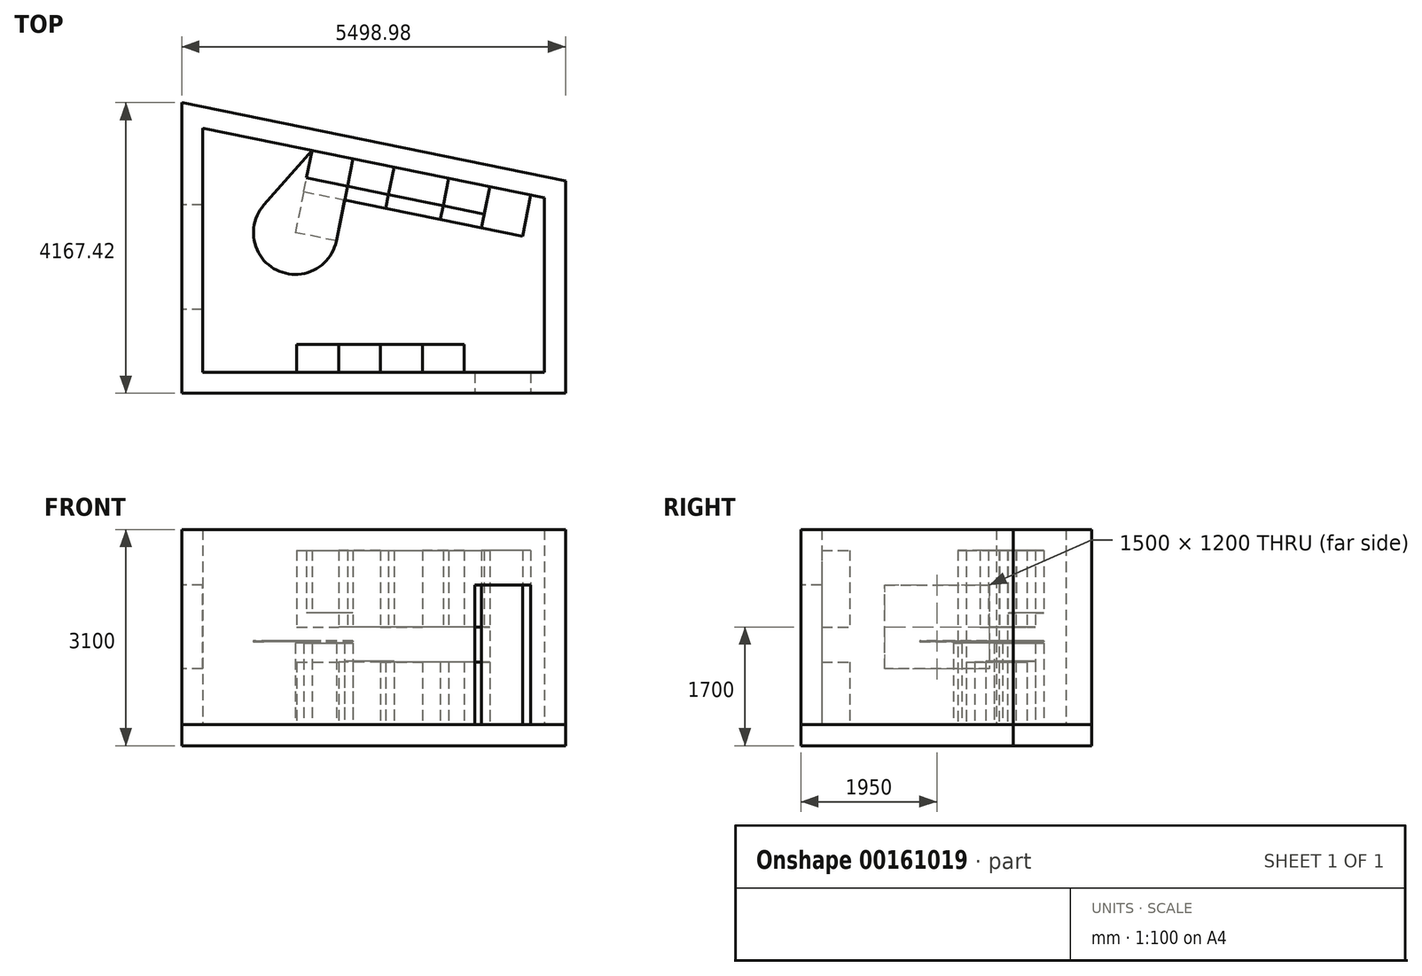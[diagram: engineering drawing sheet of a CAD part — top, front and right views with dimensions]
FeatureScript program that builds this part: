
annotation { "Feature Type Name" : "Feature", "Feature Type Description" : "" }
export const myFeature = defineFeature(function(context is Context, id is Id, definition is map)
    precondition{}
    {
        {
            var Q0;
            Q0=qCreatedBy(makeId("Top.planeOp"),FACE);
            var sketch = newSketch(context, id + "F0", { "sketchPlane" : qUnion([Q0])});
            skLineSegment(sketch, "E0", {"start": v(-2449.49, -1250) * mm, "end": v(2449.49, -1250) * mm});
            skLineSegment(sketch, "E1", {"start": v(2449.49, -1250) * mm, "end": v(2449.49, 1250) * mm});
            skLineSegment(sketch, "E2", {"start": v(2449.49, 1250) * mm, "end": v(-2449.49, 2250) * mm});
            skLineSegment(sketch, "E3", {"start": v(-2449.49, 2250) * mm, "end": v(-2449.49, -1250) * mm});
            skPoint(sketch, "E4", {"position": v(2449.49, 0) * mm});
            skLineSegment(sketch, "E5", {"start": v(2449.49, 0) * mm, "end": v(-2449.49, 0) * mm, "construction": true});
            skPoint(sketch, "E6", {"position": v(0, 0) * mm});
            skLineSegment(sketch, "E7.0", {"start": v(2749.49, 1494.95) * mm, "end": v(-2749.49, 2617.42) * mm});
            skLineSegment(sketch, "E7.1", {"start": v(2749.49, -1550) * mm, "end": v(2749.49, 1494.95) * mm});
            skLineSegment(sketch, "E7.2", {"start": v(-2749.49, -1550) * mm, "end": v(2749.49, -1550) * mm});
            skLineSegment(sketch, "E7.3", {"start": v(-2749.49, 2617.42) * mm, "end": v(-2749.49, -1550) * mm});
            skLineSegment(sketch, "E8", {"start": v(-2449.49, -250) * mm, "end": v(-2749.49, -250) * mm});
            skLineSegment(sketch, "E9", {"start": v(-2449.49, 1250) * mm, "end": v(-2749.49, 1250) * mm});
            skLineSegment(sketch, "E10", {"start": v(2249.49, -1250) * mm, "end": v(2249.49, -1550) * mm});
            skLineSegment(sketch, "E11", {"start": v(1449.49, -1250) * mm, "end": v(1449.49, -1550) * mm});
            skSolve(sketch);
        }
        {
            var Q0;
            {var subQ0=sQuery(id+"F0.wireOp",EDGE,"E8");Q0=makeQuery(id+"F0.imprint","IMPRINT",FACE,{"disambiguationData":[TD([[makeQuery(id+"F0.imprint","IMPRINT",EDGE,{"derivedFrom":subQ0}),-1.0]])]});}
            var Q1;
            {var subQ0=sQuery(id+"F0.wireOp",EDGE,"E1");Q1=makeQuery(id+"F0.imprint","IMPRINT",FACE,{"disambiguationData":[TD([[makeQuery(id+"F0.imprint","IMPRINT",EDGE,{"derivedFrom":subQ0}),1.0]])]});}
            var Q2;
            {var subQ6=sQuery(id+"F0.wireOp",EDGE,"E1");Q2=makeQuery(id+"F0.imprint","IMPRINT",FACE,{"disambiguationData":[TD([[makeQuery(id+"F0.imprint","IMPRINT",EDGE,{"derivedFrom":subQ6}),-1.0]])]});}
            var Q3;
            {var subQ0=sQuery(id+"F0.wireOp",EDGE,"E10");Q3=makeQuery(id+"F0.imprint","IMPRINT",FACE,{"disambiguationData":[TD([[makeQuery(id+"F0.imprint","IMPRINT",EDGE,{"derivedFrom":subQ0}),-1.0]])]});}
            var Q4;
            {var subQ3=sQuery(id+"F0.wireOp",EDGE,"E8");Q4=makeQuery(id+"F0.imprint","IMPRINT",FACE,{"disambiguationData":[TD([[makeQuery(id+"F0.imprint","IMPRINT",EDGE,{"derivedFrom":subQ3}),1.0]])]});}
            extrude(context, id + "F1", {"entities" : qUnion([Q0, Q1, Q2, Q3, Q4]), "oppositeDirection" : true, "depth" : 300 * mm});
        }
        {
            var Q0;
            {var subQ3=sQuery(id+"F0.wireOp",EDGE,"E8");Q0=makeQuery(id+"F0.imprint","IMPRINT",FACE,{"disambiguationData":[TD([[makeQuery(id+"F0.imprint","IMPRINT",EDGE,{"derivedFrom":subQ3}),1.0]])]});}
            var Q1;
            {var subQ0=sQuery(id+"F0.wireOp",EDGE,"E8");Q1=makeQuery(id+"F0.imprint","IMPRINT",FACE,{"disambiguationData":[TD([[makeQuery(id+"F0.imprint","IMPRINT",EDGE,{"derivedFrom":subQ0}),-1.0]])]});}
            var Q2;
            {var subQ6=sQuery(id+"F0.wireOp",EDGE,"E1");Q2=makeQuery(id+"F0.imprint","IMPRINT",FACE,{"disambiguationData":[TD([[makeQuery(id+"F0.imprint","IMPRINT",EDGE,{"derivedFrom":subQ6}),-1.0]])]});}
            var Q3;
            {var subQ0=sQuery(id+"F0.wireOp",EDGE,"E10");Q3=makeQuery(id+"F0.imprint","IMPRINT",FACE,{"disambiguationData":[TD([[makeQuery(id+"F0.imprint","IMPRINT",EDGE,{"derivedFrom":subQ0}),-1.0]])]});}
            extrude(context, id + "F2", {"entities" : qUnion([Q0, Q1, Q2, Q3]), "depth" : 2800 * mm});
        }
        {
            var Q0;
            {var subQ0=sQuery(id+"F0.wireOp",EDGE,"E10");Q0=makeQuery(id+"F0.imprint","IMPRINT",FACE,{"disambiguationData":[TD([[makeQuery(id+"F0.imprint","IMPRINT",EDGE,{"derivedFrom":subQ0}),-1.0]])]});}
            extrude(context, id + "F3", {"entities" : qUnion([Q0]), "operationType" : NewBodyOperationType.REMOVE, "depth" : 2000 * mm});
        }
        {
            var Q0;
            Q0=makeQuery(id+"F2.opExtrude","SWEPT_FACE",FACE,{"disambiguationData":[OSD([sQuery(id+"F0.wireOp",EDGE,"E7.3")])]});
            var sketch = newSketch(context, id + "F4", { "sketchPlane" : qUnion([Q0])});
            skLineSegment(sketch, "E12.0", {"start": v(1250, 2000) * mm, "end": v(1550, 2000) * mm});
            skLineSegment(sketch, "E13", {"start": v(350, 800) * mm, "end": v(350, 2000) * mm});
            skLineSegment(sketch, "E14", {"start": v(350, 2000) * mm, "end": v(-1150, 2000) * mm});
            skLineSegment(sketch, "E15", {"start": v(-1150, 2000) * mm, "end": v(-1150, 800) * mm});
            skLineSegment(sketch, "E16", {"start": v(-1150, 800) * mm, "end": v(350, 800) * mm});
            skSolve(sketch);
        }
        {
            var Q0;
            Q0=makeQuery(id+"F4.imprint","IMPRINT",FACE,{"disambiguationData":[TD([[makeQuery(id+"F4.imprint","IMPRINT",EDGE,{"derivedFrom":sQuery(id+"F4.wireOp",EDGE,"E13")}),1.0]])]});
            var Q1;
            Q1=makeQuery(id+"F2.opExtrude","SWEPT_FACE",FACE,{"disambiguationData":[OSD([sQuery(id+"F0.wireOp",EDGE,"E3")])]});
            extrude(context, id + "F5", {"entities" : qUnion([Q0]), "operationType" : NewBodyOperationType.REMOVE, "endBound" : BoundingType.UP_TO_SURFACE, "oppositeDirection" : true, "endBoundEntityFace" : qUnion([Q1]), "depth" : 25 * mm});
        }
        {
            var Q0;
            Q0=makeQuery(id+"F2.opExtrude","CAP_FACE",FACE,{"disambiguationData":[OSD([sQuery(id+"F0.wireOp",EDGE,"E0"),sQuery(id+"F0.wireOp",EDGE,"E1"),sQuery(id+"F0.wireOp",EDGE,"E2"),sQuery(id+"F0.wireOp",EDGE,"E3"),sQuery(id+"F0.wireOp",EDGE,"E7.0"),sQuery(id+"F0.wireOp",EDGE,"E7.1"),sQuery(id+"F0.wireOp",EDGE,"E7.2"),sQuery(id+"F0.wireOp",EDGE,"E7.3")])],"isStart":true});
            var sketch = newSketch(context, id + "F6", { "sketchPlane" : qUnion([Q0])});
            skLineSegment(sketch, "E17.0", {"start": v(2449.49, -1250) * mm, "end": v(-2449.49, -2250) * mm});
            skLineSegment(sketch, "E18.0", {"start": v(2449.49, 1250) * mm, "end": v(2449.49, -1250) * mm});
            skLineSegment(sketch, "E19.0", {"start": v(-2449.49, 1250) * mm, "end": v(1449.49, 1250) * mm});
            skLineSegment(sketch, "E20.0", {"start": v(1449.49, 1250) * mm, "end": v(1449.49, 1550) * mm});
            skLineSegment(sketch, "E21.0", {"start": v(-2449.49, -2250) * mm, "end": v(-2449.49, 1250) * mm});
            skLineSegment(sketch, "E22", {"start": v(2253.53, -1290) * mm, "end": v(2133.53, -702.12) * mm});
            skLineSegment(sketch, "E23", {"start": v(2133.53, -702.12) * mm, "end": v(-1001.82, -1342.12) * mm});
            skLineSegment(sketch, "E24", {"start": v(1545.65, -822.12) * mm, "end": v(1665.65, -1410) * mm});
            skLineSegment(sketch, "E25", {"start": v(1077.78, -1530) * mm, "end": v(957.78, -942.12) * mm});
            skLineSegment(sketch, "E26", {"start": v(293.94, -1690) * mm, "end": v(173.94, -1102.12) * mm});
            skLineSegment(sketch, "E27", {"start": v(-293.94, -1810) * mm, "end": v(-533.94, -634.24) * mm});
            skLineSegment(sketch, "E28", {"start": v(-881.82, -1930) * mm, "end": v(-1121.82, -754.24) * mm});
            skLineSegment(sketch, "E29", {"start": v(1299.49, 850) * mm, "end": v(-1100.51, 850) * mm});
            skLineSegment(sketch, "E30", {"start": v(1299.49, 1250) * mm, "end": v(1299.49, 850) * mm});
            skLineSegment(sketch, "E31", {"start": v(699.49, 1250) * mm, "end": v(699.49, 850) * mm});
            skLineSegment(sketch, "E32", {"start": v(99.49, 1250) * mm, "end": v(99.49, 850) * mm});
            skLineSegment(sketch, "E33", {"start": v(-500.51, 1250) * mm, "end": v(-500.51, 850) * mm});
            skPoint(sketch, "E34.orphan", {"position": v(1449.49, 850) * mm});
            skLineSegment(sketch, "E35", {"start": v(-1100.51, 850) * mm, "end": v(-1100.51, 1250) * mm});
            skCircle(sketch, "E36", {"center": v(-1121.82, -754.24) * mm, "radius": 600 * mm});
            skLineSegment(sketch, "E37", {"start": v(-881.82, -1930) * mm, "end": v(-1570.93, -1152.1) * mm});
            skLineSegment(sketch, "E38", {"start": v(-533.94, -634.24) * mm, "end": v(-1121.82, -754.24) * mm});
            skLineSegment(sketch, "E39", {"start": v(2173.53, -898.08) * mm, "end": v(-2449.49, -1841.75) * mm});
            skSolve(sketch);
        }
        {
            var Q0;
            {var subQ0=sQuery(id+"F6.wireOp",EDGE,"E22");Q0=makeQuery(id+"F6.imprint","IMPRINT",FACE,{"disambiguationData":[TD([[makeQuery(id+"F6.imprint","IMPRINT",EDGE,{"derivedFrom":subQ0}),1.0]])]});}
            extrude(context, id + "F7", {"entities" : qUnion([Q0]), "oppositeDirection" : true, "depth" : 2500 * mm});
        }
        {
            var Q0;
            {var subQ3=sQuery(id+"F6.wireOp",EDGE,"E38");Q0=makeQuery(id+"F6.imprint","IMPRINT",FACE,{"disambiguationData":[TD([[makeQuery(id+"F6.imprint","IMPRINT",EDGE,{"derivedFrom":subQ3}),1.0]])]});}
            var Q1;
            {var subQ1=sQuery(id+"F6.wireOp",EDGE,"E23");var subQ3=sQuery(id+"F6.wireOp",EDGE,"E27");var subQ4=makeQuery(id+"F6.imprint","INTERSECT",VERTEX,{"derivedFrom":[subQ1,subQ3]});Q1=makeQuery(id+"F6.imprint","IMPRINT",FACE,{"disambiguationData":[TD([[makeQuery(id+"F6.imprint","IMPRINT",EDGE,{"disambiguationData":[TD([[subQ4,-1.0]])],"derivedFrom":subQ1}),-1.0]])]});}
            extrude(context, id + "F8", {"entities" : qUnion([Q0, Q1]), "oppositeDirection" : true, "depth" : 1170 * mm});
        }
        {
            var Q0;
            {var subQ0=sQuery(id+"F6.wireOp",EDGE,"E30");Q0=makeQuery(id+"F6.imprint","IMPRINT",FACE,{"disambiguationData":[TD([[makeQuery(id+"F6.imprint","IMPRINT",EDGE,{"derivedFrom":subQ0}),-1.0]])]});}
            extrude(context, id + "F9", {"entities" : qUnion([Q0]), "oppositeDirection" : true, "depth" : 900 * mm});
        }
        {
            var Q0;
            {var subQ0=sQuery(id+"F6.wireOp",EDGE,"E31");Q0=makeQuery(id+"F6.imprint","IMPRINT",FACE,{"disambiguationData":[TD([[makeQuery(id+"F6.imprint","IMPRINT",EDGE,{"derivedFrom":subQ0}),-1.0]])]});}
            extrude(context, id + "F10", {"entities" : qUnion([Q0]), "oppositeDirection" : true, "depth" : 900 * mm});
        }
        {
            var Q0;
            {var subQ0=sQuery(id+"F6.wireOp",EDGE,"E32");Q0=makeQuery(id+"F6.imprint","IMPRINT",FACE,{"disambiguationData":[TD([[makeQuery(id+"F6.imprint","IMPRINT",EDGE,{"derivedFrom":subQ0}),-1.0]])]});}
            extrude(context, id + "F11", {"entities" : qUnion([Q0]), "oppositeDirection" : true, "depth" : 900 * mm});
        }
        {
            var Q0;
            {var subQ0=sQuery(id+"F6.wireOp",EDGE,"E33");Q0=makeQuery(id+"F6.imprint","IMPRINT",FACE,{"disambiguationData":[TD([[makeQuery(id+"F6.imprint","IMPRINT",EDGE,{"derivedFrom":subQ0}),-1.0]])]});}
            extrude(context, id + "F12", {"entities" : qUnion([Q0]), "oppositeDirection" : true, "depth" : 900 * mm});
        }
        {
            var Q0;
            {var subQ0=sQuery(id+"F6.wireOp",EDGE,"E30");Q0=makeQuery(id+"F6.imprint","IMPRINT",FACE,{"disambiguationData":[TD([[makeQuery(id+"F6.imprint","IMPRINT",EDGE,{"derivedFrom":subQ0}),-1.0]])]});}
            extrude(context, id + "F13", {"entities" : qUnion([Q0]), "oppositeDirection" : true, "depth" : 2500 * mm, "hasSecondDirection" : true, "secondDirectionOppositeDirection" : true, "secondDirectionDepth" : 1400 * mm});
        }
        {
            var Q0;
            {var subQ0=sQuery(id+"F6.wireOp",EDGE,"E31");Q0=makeQuery(id+"F6.imprint","IMPRINT",FACE,{"disambiguationData":[TD([[makeQuery(id+"F6.imprint","IMPRINT",EDGE,{"derivedFrom":subQ0}),-1.0]])]});}
            extrude(context, id + "F14", {"entities" : qUnion([Q0]), "oppositeDirection" : true, "depth" : 2500 * mm, "hasSecondDirection" : true, "secondDirectionOppositeDirection" : true, "secondDirectionDepth" : 1400 * mm});
        }
        {
            var Q0;
            {var subQ0=sQuery(id+"F6.wireOp",EDGE,"E32");Q0=makeQuery(id+"F6.imprint","IMPRINT",FACE,{"disambiguationData":[TD([[makeQuery(id+"F6.imprint","IMPRINT",EDGE,{"derivedFrom":subQ0}),-1.0]])]});}
            extrude(context, id + "F15", {"entities" : qUnion([Q0]), "oppositeDirection" : true, "depth" : 2500 * mm, "hasSecondDirection" : true, "secondDirectionOppositeDirection" : true, "secondDirectionDepth" : 1400 * mm});
        }
        {
            var Q0;
            {var subQ0=sQuery(id+"F6.wireOp",EDGE,"E33");Q0=makeQuery(id+"F6.imprint","IMPRINT",FACE,{"disambiguationData":[TD([[makeQuery(id+"F6.imprint","IMPRINT",EDGE,{"derivedFrom":subQ0}),-1.0]])]});}
            extrude(context, id + "F16", {"entities" : qUnion([Q0]), "oppositeDirection" : true, "depth" : 2500 * mm, "hasSecondDirection" : true, "secondDirectionOppositeDirection" : true, "secondDirectionDepth" : 1400 * mm});
        }
        {
            var Q0;
            {var subQ0=sQuery(id+"F6.wireOp",EDGE,"E24");Q0=makeQuery(id+"F6.imprint","IMPRINT",FACE,{"disambiguationData":[TD([[makeQuery(id+"F6.imprint","IMPRINT",EDGE,{"derivedFrom":subQ0}),-1.0]])]});}
            extrude(context, id + "F17", {"entities" : qUnion([Q0]), "oppositeDirection" : true, "depth" : 900 * mm});
        }
        {
            var Q0;
            {var subQ0=sQuery(id+"F6.wireOp",EDGE,"E25");Q0=makeQuery(id+"F6.imprint","IMPRINT",FACE,{"disambiguationData":[TD([[makeQuery(id+"F6.imprint","IMPRINT",EDGE,{"derivedFrom":subQ0}),1.0]])]});}
            extrude(context, id + "F18", {"entities" : qUnion([Q0]), "oppositeDirection" : true, "depth" : 900 * mm});
        }
        {
            var Q0;
            {var subQ0=sQuery(id+"F6.wireOp",EDGE,"E26");Q0=makeQuery(id+"F6.imprint","IMPRINT",FACE,{"disambiguationData":[TD([[makeQuery(id+"F6.imprint","IMPRINT",EDGE,{"derivedFrom":subQ0}),1.0]])]});}
            extrude(context, id + "F19", {"entities" : qUnion([Q0]), "oppositeDirection" : true, "depth" : 910 * mm});
        }
        {
            var Q0;
            {var subQ0=sQuery(id+"F6.wireOp",EDGE,"E27");var subQ1=sQuery(id+"F6.wireOp",EDGE,"E17.0");var subQ2=makeQuery(id+"F6.imprint","INTERSECT",VERTEX,{"derivedFrom":[subQ1,subQ0]});Q0=makeQuery(id+"F6.imprint","IMPRINT",FACE,{"disambiguationData":[TD([[makeQuery(id+"F6.imprint","IMPRINT",EDGE,{"disambiguationData":[TD([[subQ2,-1.0]])],"derivedFrom":subQ0}),1.0]])]});}
            var Q1;
            {var subQ1=sQuery(id+"F6.wireOp",EDGE,"E23");var subQ3=sQuery(id+"F6.wireOp",EDGE,"E27");var subQ4=makeQuery(id+"F6.imprint","INTERSECT",VERTEX,{"derivedFrom":[subQ1,subQ3]});Q1=makeQuery(id+"F6.imprint","IMPRINT",FACE,{"disambiguationData":[TD([[makeQuery(id+"F6.imprint","IMPRINT",EDGE,{"disambiguationData":[TD([[subQ4,1.0]])],"derivedFrom":subQ3}),1.0]])]});}
            var Q2;
            Q2=makeQuery(id+"F8.opExtrude","CAP_FACE",FACE,{"disambiguationData":[OSD([sQuery(id+"F6.wireOp",EDGE,"E23"),sQuery(id+"F6.wireOp",EDGE,"E27"),sQuery(id+"F6.wireOp",EDGE,"E28"),sQuery(id+"F6.wireOp",EDGE,"E38")])],"isStart":false});
            extrude(context, id + "F20", {"entities" : qUnion([Q0, Q1]), "endBound" : BoundingType.UP_TO_SURFACE, "oppositeDirection" : true, "endBoundEntityFace" : qUnion([Q2]), "depth" : 25 * mm});
        }
        {
            var Q0;
            {var subQ3=sQuery(id+"F6.wireOp",EDGE,"E38");Q0=makeQuery(id+"F6.imprint","IMPRINT",FACE,{"disambiguationData":[TD([[makeQuery(id+"F6.imprint","IMPRINT",EDGE,{"derivedFrom":subQ3}),-1.0]])]});}
            var Q1;
            {var subQ3=sQuery(id+"F6.wireOp",EDGE,"E38");Q1=makeQuery(id+"F6.imprint","IMPRINT",FACE,{"disambiguationData":[TD([[makeQuery(id+"F6.imprint","IMPRINT",EDGE,{"derivedFrom":subQ3}),1.0]])]});}
            var Q2;
            {var subQ1=sQuery(id+"F6.wireOp",EDGE,"E23");var subQ3=sQuery(id+"F6.wireOp",EDGE,"E27");var subQ4=makeQuery(id+"F6.imprint","INTERSECT",VERTEX,{"derivedFrom":[subQ1,subQ3]});Q2=makeQuery(id+"F6.imprint","IMPRINT",FACE,{"disambiguationData":[TD([[makeQuery(id+"F6.imprint","IMPRINT",EDGE,{"disambiguationData":[TD([[subQ4,-1.0]])],"derivedFrom":subQ1}),-1.0]])]});}
            var Q3;
            {var subQ1=sQuery(id+"F6.wireOp",EDGE,"E23");var subQ3=sQuery(id+"F6.wireOp",EDGE,"E27");var subQ4=makeQuery(id+"F6.imprint","INTERSECT",VERTEX,{"derivedFrom":[subQ1,subQ3]});Q3=makeQuery(id+"F6.imprint","IMPRINT",FACE,{"disambiguationData":[TD([[makeQuery(id+"F6.imprint","IMPRINT",EDGE,{"disambiguationData":[TD([[subQ4,1.0]])],"derivedFrom":subQ3}),1.0]])]});}
            var Q4;
            {var subQ0=sQuery(id+"F6.wireOp",EDGE,"E27");var subQ1=sQuery(id+"F6.wireOp",EDGE,"E17.0");var subQ2=makeQuery(id+"F6.imprint","INTERSECT",VERTEX,{"derivedFrom":[subQ1,subQ0]});Q4=makeQuery(id+"F6.imprint","IMPRINT",FACE,{"disambiguationData":[TD([[makeQuery(id+"F6.imprint","IMPRINT",EDGE,{"disambiguationData":[TD([[subQ2,-1.0]])],"derivedFrom":subQ0}),1.0]])]});}
            var Q5;
            {var subQ0=sQuery(id+"F6.wireOp",EDGE,"E36");var subQ5=sQuery(id+"F6.wireOp",EDGE,"E37");var subQ6=makeQuery(id+"F6.imprint","INTERSECT",VERTEX,{"derivedFrom":[subQ0,subQ5]});Q5=makeQuery(id+"F6.imprint","IMPRINT",FACE,{"disambiguationData":[TD([[makeQuery(id+"F6.imprint","IMPRINT",EDGE,{"disambiguationData":[TD([[subQ6,1.0]])],"derivedFrom":subQ5}),-1.0]])]});}
            var Q6;
            {var subQ0=sQuery(id+"F6.wireOp",EDGE,"E37");var subQ3=sQuery(id+"F6.wireOp",EDGE,"E39");var subQ5=makeQuery(id+"F6.imprint","INTERSECT",VERTEX,{"derivedFrom":[subQ0,subQ3]});Q6=makeQuery(id+"F6.imprint","IMPRINT",FACE,{"disambiguationData":[TD([[makeQuery(id+"F6.imprint","IMPRINT",EDGE,{"disambiguationData":[TD([[subQ5,1.0]])],"derivedFrom":subQ3}),1.0]])]});}
            var Q7;
            Q7=makeQuery(id+"F8.opExtrude","CAP_FACE",FACE,{"disambiguationData":[OSD([sQuery(id+"F6.wireOp",EDGE,"E23"),sQuery(id+"F6.wireOp",EDGE,"E27"),sQuery(id+"F6.wireOp",EDGE,"E28"),sQuery(id+"F6.wireOp",EDGE,"E38")])],"isStart":false});
            extrude(context, id + "F21", {"entities" : qUnion([Q0, Q1, Q2, Q3, Q4, Q5, Q6]), "oppositeDirection" : true, "depth" : 1200 * mm, "hasSecondDirection" : true, "secondDirectionOppositeDirection" : true, "secondDirectionBoundEntityFace" : qUnion([Q7]), "secondDirectionDepth" : 1190 * mm});
        }
        {
            var Q0;
            {var subQ0=sQuery(id+"F6.wireOp",EDGE,"E24");var subQ1=sQuery(id+"F6.wireOp",EDGE,"E17.0");var subQ2=makeQuery(id+"F6.imprint","INTERSECT",VERTEX,{"derivedFrom":[subQ1,subQ0]});Q0=makeQuery(id+"F6.imprint","IMPRINT",FACE,{"disambiguationData":[TD([[makeQuery(id+"F6.imprint","IMPRINT",EDGE,{"disambiguationData":[TD([[subQ2,-1.0]])],"derivedFrom":subQ1}),-1.0]])]});}
            var Q1;
            Q1=makeQuery(id+"F7.opExtrude","CAP_FACE",FACE,{"disambiguationData":[OSD([sQuery(id+"F6.wireOp",EDGE,"E17.0"),sQuery(id+"F6.wireOp",EDGE,"E22"),sQuery(id+"F6.wireOp",EDGE,"E23"),sQuery(id+"F6.wireOp",EDGE,"E24")])],"isStart":false});
            extrude(context, id + "F22", {"entities" : qUnion([Q0]), "endBound" : BoundingType.UP_TO_SURFACE, "oppositeDirection" : true, "endBoundEntityFace" : qUnion([Q1]), "depth" : 25 * mm, "hasSecondDirection" : true, "secondDirectionOppositeDirection" : true, "secondDirectionDepth" : 1400 * mm});
        }
        {
            var Q0;
            {var subQ0=sQuery(id+"F6.wireOp",EDGE,"E25");var subQ1=sQuery(id+"F6.wireOp",EDGE,"E17.0");var subQ2=makeQuery(id+"F6.imprint","INTERSECT",VERTEX,{"derivedFrom":[subQ1,subQ0]});Q0=makeQuery(id+"F6.imprint","IMPRINT",FACE,{"disambiguationData":[TD([[makeQuery(id+"F6.imprint","IMPRINT",EDGE,{"disambiguationData":[TD([[subQ2,-1.0]])],"derivedFrom":subQ1}),-1.0]])]});}
            var Q1;
            Q1=makeQuery(id+"F22.opExtrude","CAP_FACE",FACE,{"disambiguationData":[OSD([sQuery(id+"F6.wireOp",EDGE,"E17.0"),sQuery(id+"F6.wireOp",EDGE,"E22"),sQuery(id+"F6.wireOp",EDGE,"E23"),sQuery(id+"F6.wireOp",EDGE,"E24")])],"isStart":false});
            extrude(context, id + "F23", {"entities" : qUnion([Q0]), "endBound" : BoundingType.UP_TO_SURFACE, "oppositeDirection" : true, "endBoundEntityFace" : qUnion([Q1]), "depth" : 25 * mm, "hasSecondDirection" : true, "secondDirectionOppositeDirection" : true, "secondDirectionDepth" : 1400 * mm});
        }
        {
            var Q0;
            {var subQ0=sQuery(id+"F6.wireOp",EDGE,"E26");var subQ1=sQuery(id+"F6.wireOp",EDGE,"E17.0");var subQ2=makeQuery(id+"F6.imprint","INTERSECT",VERTEX,{"derivedFrom":[subQ1,subQ0]});Q0=makeQuery(id+"F6.imprint","IMPRINT",FACE,{"disambiguationData":[TD([[makeQuery(id+"F6.imprint","IMPRINT",EDGE,{"disambiguationData":[TD([[subQ2,-1.0]])],"derivedFrom":subQ1}),-1.0]])]});}
            var Q1;
            Q1=makeQuery(id+"F7.opExtrude","CAP_FACE",FACE,{"disambiguationData":[OSD([sQuery(id+"F6.wireOp",EDGE,"E17.0"),sQuery(id+"F6.wireOp",EDGE,"E22"),sQuery(id+"F6.wireOp",EDGE,"E23"),sQuery(id+"F6.wireOp",EDGE,"E24")])],"isStart":false});
            extrude(context, id + "F24", {"entities" : qUnion([Q0]), "endBound" : BoundingType.UP_TO_SURFACE, "oppositeDirection" : true, "endBoundEntityFace" : qUnion([Q1]), "depth" : 25 * mm, "hasSecondDirection" : true, "secondDirectionOppositeDirection" : true, "secondDirectionDepth" : 1400 * mm});
        }
        {
            var Q0;
            {var subQ0=sQuery(id+"F6.wireOp",EDGE,"E27");var subQ1=sQuery(id+"F6.wireOp",EDGE,"E17.0");var subQ2=makeQuery(id+"F6.imprint","INTERSECT",VERTEX,{"derivedFrom":[subQ1,subQ0]});Q0=makeQuery(id+"F6.imprint","IMPRINT",FACE,{"disambiguationData":[TD([[makeQuery(id+"F6.imprint","IMPRINT",EDGE,{"disambiguationData":[TD([[subQ2,-1.0]])],"derivedFrom":subQ0}),1.0]])]});}
            var Q1;
            Q1=makeQuery(id+"F7.opExtrude","CAP_FACE",FACE,{"disambiguationData":[OSD([sQuery(id+"F6.wireOp",EDGE,"E17.0"),sQuery(id+"F6.wireOp",EDGE,"E22"),sQuery(id+"F6.wireOp",EDGE,"E23"),sQuery(id+"F6.wireOp",EDGE,"E24")])],"isStart":false});
            extrude(context, id + "F25", {"entities" : qUnion([Q0]), "endBound" : BoundingType.UP_TO_SURFACE, "oppositeDirection" : true, "endBoundEntityFace" : qUnion([Q1]), "depth" : 25 * mm, "hasSecondDirection" : true, "secondDirectionOppositeDirection" : true, "secondDirectionDepth" : 1600 * mm});
        }
    });
